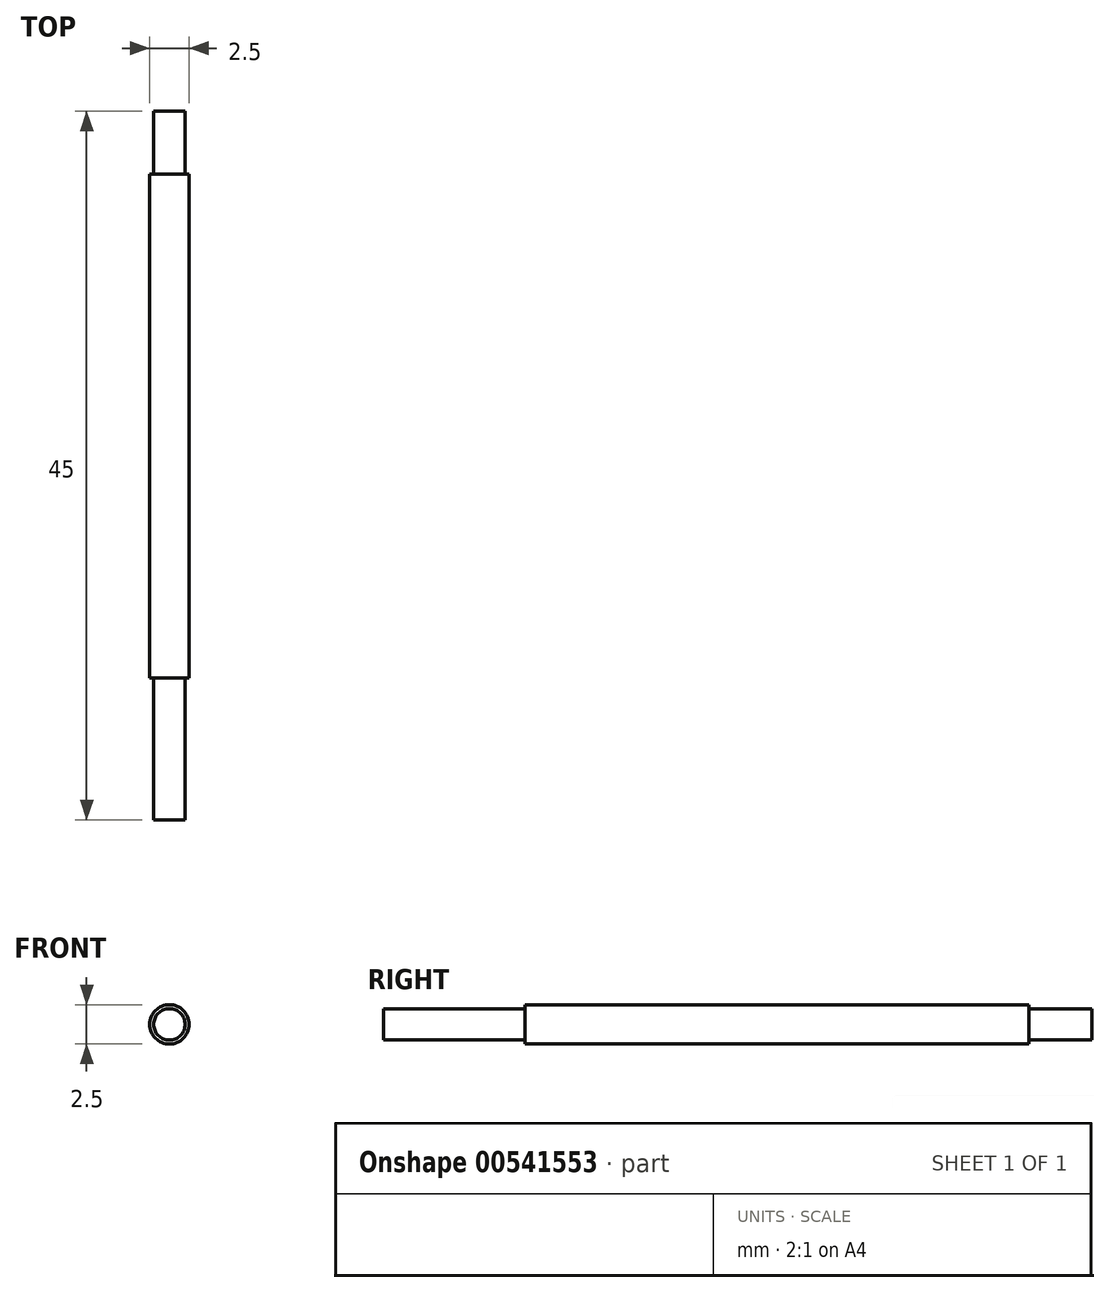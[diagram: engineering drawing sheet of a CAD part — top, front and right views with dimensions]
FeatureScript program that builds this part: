
annotation { "Feature Type Name" : "Feature", "Feature Type Description" : "" }
export const myFeature = defineFeature(function(context is Context, id is Id, definition is map)
    precondition{}
    {
        {
            var Q0;
            Q0=qCreatedBy(makeId("Front.planeOp"),FACE);
            var sketch = newSketch(context, id + "F0", { "sketchPlane" : qUnion([Q0])});
            skCircle(sketch, "E0", {"center": v(0, 0) * mm, "radius": 1.25 * mm});
            skSolve(sketch);
        }
        {
            var Q0;
            Q0=makeQuery(id+"F0.imprint","IMPRINT",FACE,{"disambiguationData":[TD([[makeQuery(id+"F0.imprint","IMPRINT",EDGE,{"derivedFrom":sQuery(id+"F0.wireOp",EDGE,"E0")}),1.0]])]});
            extrude(context, id + "F1", {"entities" : qUnion([Q0]), "depth" : 32 * mm, "offsetDistance" : 25 * mm});
        }
        {
            var Q0;
            Q0=makeQuery(id+"F1.opExtrude","CAP_FACE",FACE,{"disambiguationData":[OSD([sQuery(id+"F0.wireOp",EDGE,"E0")])],"isStart":false});
            var sketch = newSketch(context, id + "F2", { "sketchPlane" : qUnion([Q0])});
            skLineSegment(sketch, "E1", {"start": v(0, 1.25) * mm, "end": v(0, -1.25) * mm, "construction": true});
            skLineSegment(sketch, "E2", {"start": v(-1.25, 0) * mm, "end": v(1.25, 0) * mm, "construction": true});
            skCircle(sketch, "E3", {"center": v(0, 0) * mm, "radius": 1 * mm});
            skSolve(sketch);
        }
        {
            var Q0;
            Q0=makeQuery(id+"F2.imprint","IMPRINT",FACE,{"disambiguationData":[TD([[makeQuery(id+"F2.imprint","IMPRINT",EDGE,{"derivedFrom":sQuery(id+"F2.wireOp",EDGE,"E3")}),1.0]])]});
            extrude(context, id + "F3", {"entities" : qUnion([Q0]), "operationType" : NewBodyOperationType.ADD, "depth" : 9 * mm, "offsetDistance" : 25 * mm});
        }
        {
            var Q0;
            Q0=makeQuery(id+"F1.opExtrude","CAP_FACE",FACE,{"disambiguationData":[OSD([sQuery(id+"F0.wireOp",EDGE,"E0")])],"isStart":true});
            var sketch = newSketch(context, id + "F4", { "sketchPlane" : qUnion([Q0])});
            skLineSegment(sketch, "E4", {"start": v(0, 1.25) * mm, "end": v(0, -1.25) * mm, "construction": true});
            skLineSegment(sketch, "E5", {"start": v(-1.25, 0) * mm, "end": v(1.25, 0) * mm, "construction": true});
            skCircle(sketch, "E6", {"center": v(0, 0) * mm, "radius": 1 * mm});
            skSolve(sketch);
        }
        {
            var Q0;
            Q0=makeQuery(id+"F4.imprint","IMPRINT",FACE,{"disambiguationData":[TD([[makeQuery(id+"F4.imprint","IMPRINT",EDGE,{"derivedFrom":sQuery(id+"F4.wireOp",EDGE,"E6")}),1.0]])]});
            extrude(context, id + "F5", {"entities" : qUnion([Q0]), "operationType" : NewBodyOperationType.ADD, "depth" : 4 * mm, "offsetDistance" : 25 * mm});
        }
    });
